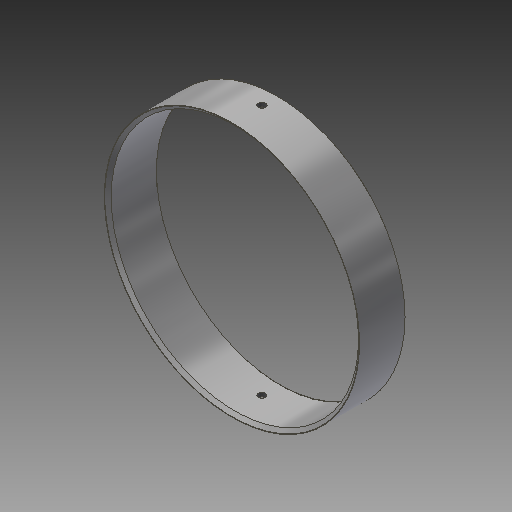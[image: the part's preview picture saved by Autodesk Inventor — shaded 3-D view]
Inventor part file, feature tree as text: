
AUTODESK INVENTOR PART (.ipt)
format: ipt  version: 2017.3 (Build 213257000, 257)  size: 131,072 bytes
history: native  units: in
note: dims shown in document units (in); Inventor stores cm internally (conversion verified against a paired STEP export)
features: chamfer x2, sketch x2, extrude x1, plane x1, hole x1, pattern_circular x1
ambient origin geometry x8: Origin, YZ Plane, XZ Plane, XY Plane, X Axis, Y Axis, Z Axis, Center Point
bodies: Solid1 (feature_tree)
feature tree (8):
  extrude  "Extrusion1"  Depth=31.0in
  chamfer  "Chamfer1"  Distance=6.0394in
  chamfer  "Chamfer2"  Distance=0.125in
  plane  "Work Plane1"
  hole  "Hole1"  [1 undecoded]
  pattern_circular  "Circular Pattern1"  [2 undecoded]
  sketch  "Sketch1"  dims[d0=32.0in d1=31.0in d2=6.0394in d3=0.0in]
  sketch  "Sketch2"  dims[d4=0.4375in d5=0.125in d6=0.2577in d7=0.4375in d8=0.125in d9=0.2749in d10=2.2812in d11=0.891in d12=0.553in d13=0.0246in d14=0.897in d15=0.375in d16=0.25in d17=0.5635in d18=0.91in d19=0.8108in d20=0.7874in d21=360.0deg]
note: 3 required parameter values undecoded (feature->parameter linkage not recoverable at this tier; creation-order binding heuristic only, values carry confidence <= 0.55)
